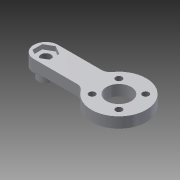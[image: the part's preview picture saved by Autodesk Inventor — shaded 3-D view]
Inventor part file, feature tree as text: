
AUTODESK INVENTOR PART (.ipt)
format: ipt  version: 2014 (Build 180170000, 170)  size: 207,360 bytes
history: native  units: mm
features: extrude x5, sketch x5, other x1, fillet x1
ambient origin geometry x8: Origin, YZ Plane, XZ Plane, XY Plane, X Axis, Y Axis, Z Axis, Center Point
bodies: Body1 (feature_tree)
feature tree (12):
  other  "ソリッド1"
  extrude  "押し出し1"  Depth=24.0mm
  extrude  "押し出し2"  Depth=4.0mm
  extrude  "押し出し3"  Depth=3.2mm
  extrude  "押し出し4"  Depth=8.1mm
  fillet  "フィレット1"  Radius=3.5mm
  extrude  "押し出し5"  Depth=18.0mm
  sketch  "スケッチ1"
  sketch  "スケッチ3"
  sketch  "スケッチ4"
  sketch  "スケッチ5"
  sketch  "スケッチ6"
